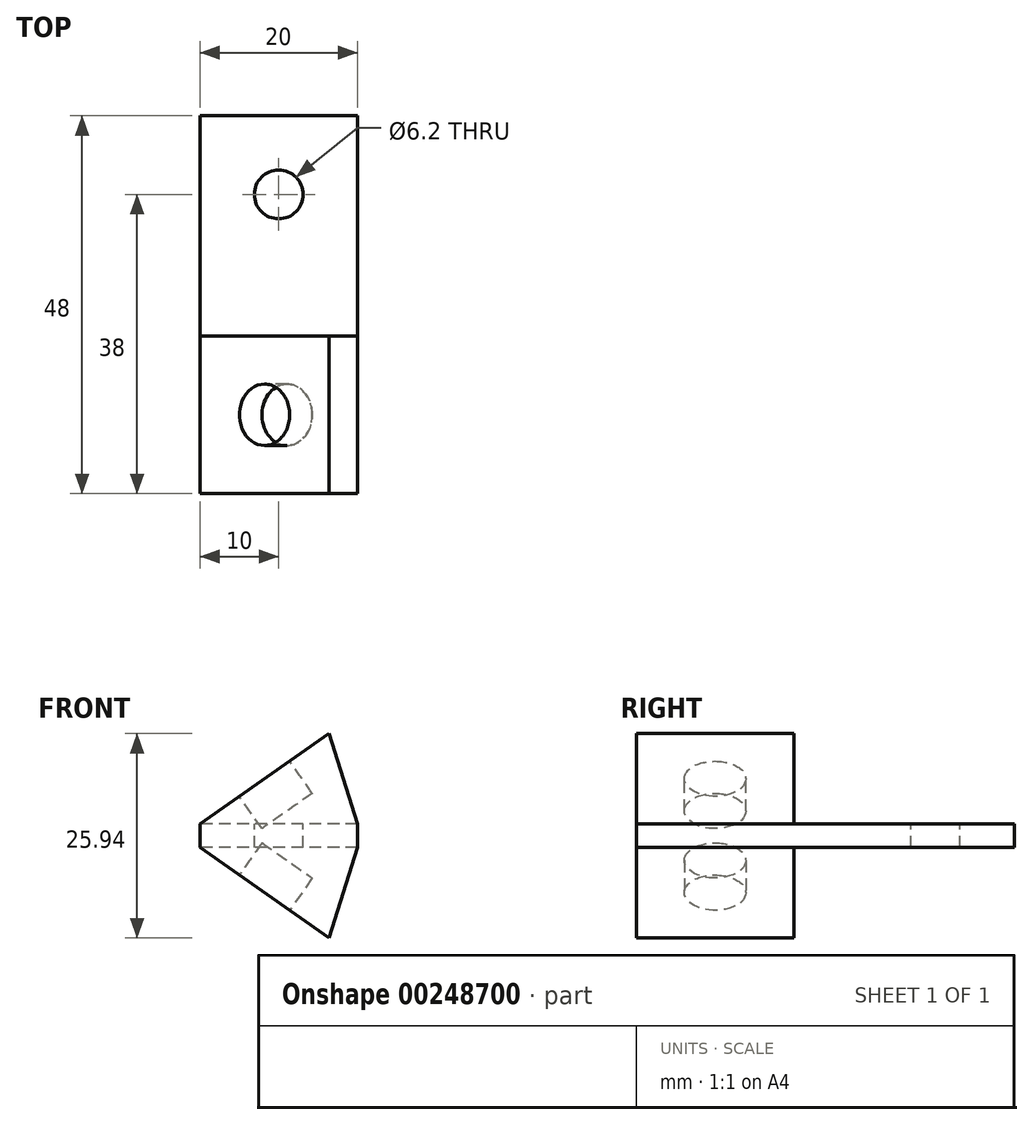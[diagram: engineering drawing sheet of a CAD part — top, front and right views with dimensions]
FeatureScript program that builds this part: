
annotation { "Feature Type Name" : "Feature", "Feature Type Description" : "" }
export const myFeature = defineFeature(function(context is Context, id is Id, definition is map)
    precondition{}
    {
        {
            var Q0;
            Q0=qCreatedBy(makeId("Top.planeOp"),FACE);
            var sketch = newSketch(context, id + "F0", { "sketchPlane" : qUnion([Q0])});
            skLineSegment(sketch, "E0.bottom", {"start": v(10, -24) * mm, "end": v(-10, -24) * mm});
            skLineSegment(sketch, "E0.top", {"start": v(10, 24) * mm, "end": v(-10, 24) * mm});
            skLineSegment(sketch, "E0.left", {"start": v(10, -24) * mm, "end": v(10, 24) * mm});
            skLineSegment(sketch, "E0.right", {"start": v(-10, -24) * mm, "end": v(-10, 24) * mm});
            skPoint(sketch, "E0.middle", {"position": v(0, 0) * mm});
            skSolve(sketch);
        }
        {
            var Q0;
            Q0 = qSketchRegion(id + "F0", true);
            extrude(context, id + "F1", {"entities" : qUnion([Q0]), "depth" : 3 * mm});
        }
        {
            var Q0;
            Q0=makeQuery(id+"F1.opExtrude","CAP_FACE",FACE,{"disambiguationData":[OSD([sQuery(id+"F0.wireOp",EDGE,"E0.bottom"),sQuery(id+"F0.wireOp",EDGE,"E0.top"),sQuery(id+"F0.wireOp",EDGE,"E0.left"),sQuery(id+"F0.wireOp",EDGE,"E0.right")])],"isStart":false});
            var sketch = newSketch(context, id + "F2", { "sketchPlane" : qUnion([Q0])});
            skCircle(sketch, "E1", {"center": v(0, 14) * mm, "radius": 3.1 * mm});
            skPoint(sketch, "E1.centerSnap0", {"position": v(0, 24) * mm});
            skSolve(sketch);
        }
        {
            var Q0;
            Q0 = qSketchRegion(id + "F2", true);
            extrude(context, id + "F3", {"entities" : qUnion([Q0]), "operationType" : NewBodyOperationType.REMOVE, "oppositeDirection" : true, "depth" : 25 * mm});
        }
        {
            var Q0;
            Q0=makeQuery(id+"F1.opExtrude","SWEPT_FACE",FACE,{"disambiguationData":[OSD([sQuery(id+"F0.wireOp",EDGE,"E0.bottom")])]});
            var sketch = newSketch(context, id + "F4", { "sketchPlane" : qUnion([Q0])});
            skLineSegment(sketch, "E2", {"start": v(-10, 3) * mm, "end": v(6.38, 14.47) * mm});
            skLineSegment(sketch, "E3", {"start": v(10, 3) * mm, "end": v(6.38, 14.47) * mm});
            skLineSegment(sketch, "E4", {"start": v(-10, 0) * mm, "end": v(6.38, -11.47) * mm});
            skLineSegment(sketch, "E5", {"start": v(6.38, -11.47) * mm, "end": v(10, 0) * mm});
            skSolve(sketch);
        }
        {
            var Q0;
            Q0=makeQuery(id+"F4.imprint","IMPRINT",FACE,{"disambiguationData":[TD([[makeQuery(id+"F4.imprint","IMPRINT",EDGE,{"derivedFrom":sQuery(id+"F4.wireOp",EDGE,"E2")}),-1.0]])]});
            var Q1;
            Q1=makeQuery(id+"F4.imprint","IMPRINT",FACE,{"disambiguationData":[TD([[makeQuery(id+"F4.imprint","IMPRINT",EDGE,{"derivedFrom":sQuery(id+"F4.wireOp",EDGE,"E4")}),1.0]])]});
            extrude(context, id + "F5", {"entities" : qUnion([Q0, Q1]), "operationType" : NewBodyOperationType.ADD, "oppositeDirection" : true, "depth" : 20 * mm});
        }
        {
            var Q0;
            Q0=makeQuery(id+"F5.opExtrude","SWEPT_FACE",FACE,{"disambiguationData":[OSD([sQuery(id+"F4.wireOp",EDGE,"E2")])]});
            var sketch = newSketch(context, id + "F6", { "sketchPlane" : qUnion([Q0])});
            skCircle(sketch, "E6", {"center": v(3.53, -14) * mm, "radius": 3.9 * mm});
            skPoint(sketch, "E6.centerSnap0", {"position": v(13.53, -14) * mm});
            skPoint(sketch, "E6.centerSnap1", {"position": v(3.53, -4) * mm});
            skSolve(sketch);
        }
        {
            var Q0;
            Q0 = qSketchRegion(id + "F6", true);
            extrude(context, id + "F7", {"entities" : qUnion([Q0]), "operationType" : NewBodyOperationType.REMOVE, "oppositeDirection" : true, "depth" : 5 * mm});
        }
        {
            var Q0;
            Q0=makeQuery(id+"F5.opExtrude","SWEPT_FACE",FACE,{"disambiguationData":[OSD([sQuery(id+"F4.wireOp",EDGE,"E4")])]});
            var sketch = newSketch(context, id + "F8", { "sketchPlane" : qUnion([Q0])});
            skCircle(sketch, "E7", {"center": v(1.8, 14) * mm, "radius": 3.9 * mm});
            skPoint(sketch, "E7.centerSnap0", {"position": v(11.8, 14) * mm});
            skPoint(sketch, "E7.centerSnap1", {"position": v(1.8, 24) * mm});
            skSolve(sketch);
        }
        {
            var Q0;
            Q0 = qSketchRegion(id + "F8", true);
            extrude(context, id + "F9", {"entities" : qUnion([Q0]), "operationType" : NewBodyOperationType.REMOVE, "oppositeDirection" : true, "depth" : 5 * mm});
        }
    });
